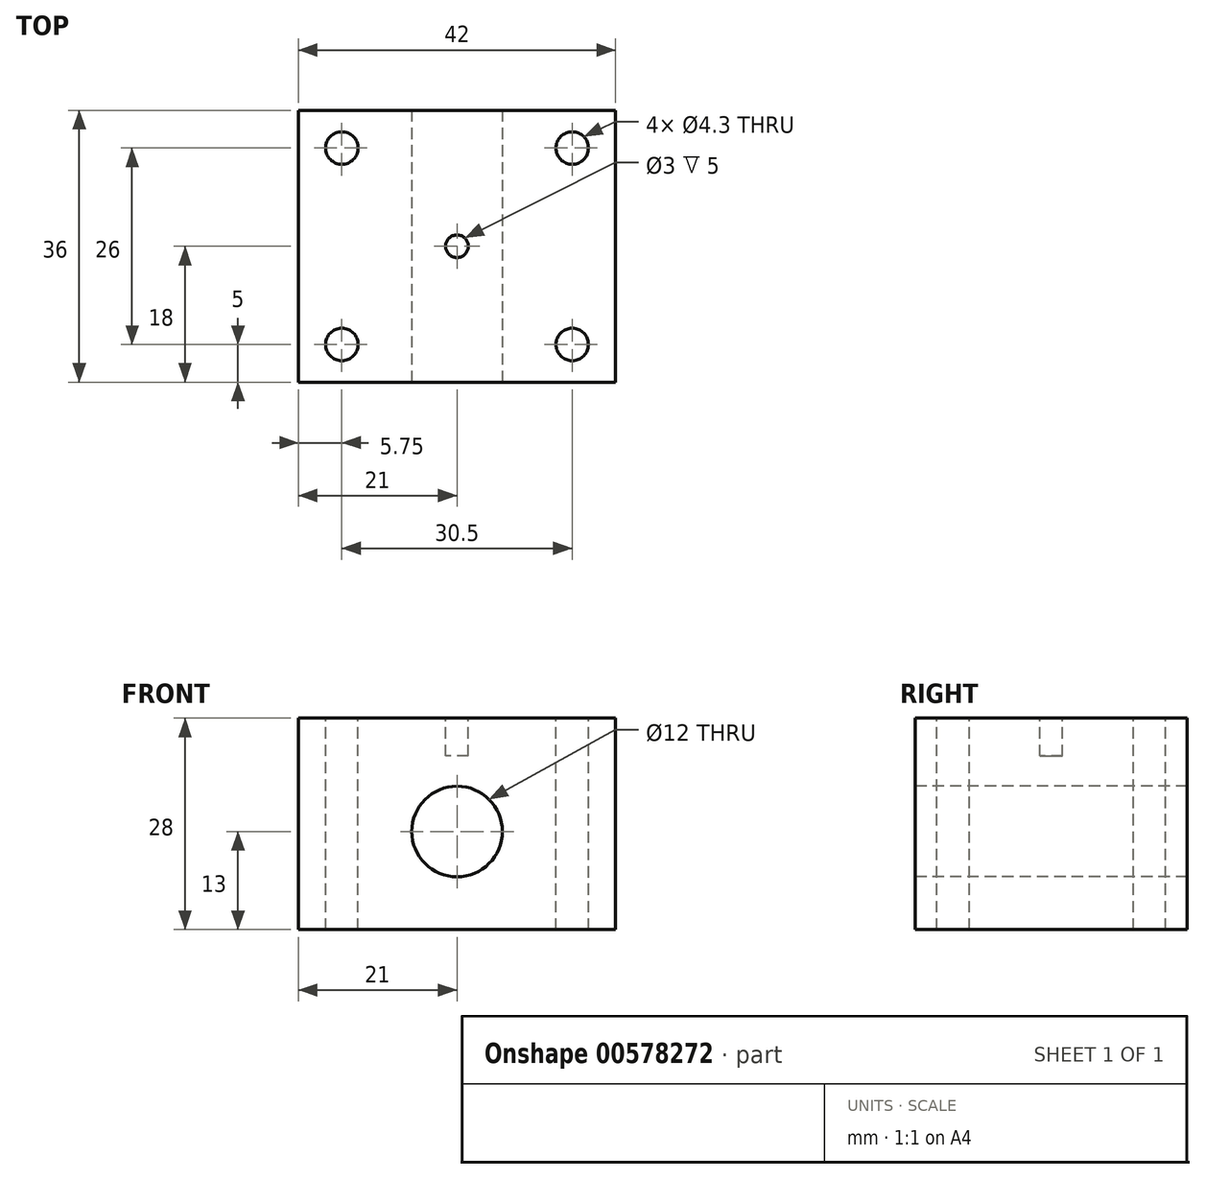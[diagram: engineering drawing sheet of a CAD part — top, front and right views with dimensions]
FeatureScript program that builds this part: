
annotation { "Feature Type Name" : "Feature", "Feature Type Description" : "" }
export const myFeature = defineFeature(function(context is Context, id is Id, definition is map)
    precondition{}
    {
        {
            var Q0;
            Q0=qCreatedBy(makeId("Top.planeOp"),FACE);
            var sketch = newSketch(context, id + "F0", { "sketchPlane" : qUnion([Q0])});
            skLineSegment(sketch, "E0.bottom", {"start": v(-21, 18) * mm, "end": v(21, 18) * mm});
            skLineSegment(sketch, "E0.top", {"start": v(-21, -18) * mm, "end": v(21, -18) * mm});
            skLineSegment(sketch, "E0.left", {"start": v(-21, 18) * mm, "end": v(-21, -18) * mm});
            skLineSegment(sketch, "E0.right", {"start": v(21, 18) * mm, "end": v(21, -18) * mm});
            skPoint(sketch, "E0.middle", {"position": v(0, 0) * mm});
            skCircle(sketch, "E1", {"center": v(-15.25, 13) * mm, "radius": 2.15 * mm});
            skCircle(sketch, "E2.MirrorC", {"center": v(15.25, 13) * mm, "radius": 2.15 * mm});
            skCircle(sketch, "E3.MirrorC", {"center": v(-15.25, -13) * mm, "radius": 2.15 * mm});
            skCircle(sketch, "E4.MirrorC", {"center": v(15.25, -13) * mm, "radius": 2.15 * mm});
            skSolve(sketch);
        }
        {
            var Q0;
            Q0 = qSketchRegion(id + "F0", true);
            extrude(context, id + "F1", {"entities" : qUnion([Q0]), "oppositeDirection" : true, "depth" : 28 * mm, "offsetDistance" : 25 * mm});
        }
        {
            var Q0;
            Q0=makeQuery(id+"F1.opExtrude","SWEPT_FACE",FACE,{"disambiguationData":[OSD([sQuery(id+"F0.wireOp",EDGE,"E0.top")])]});
            var sketch = newSketch(context, id + "F2", { "sketchPlane" : qUnion([Q0])});
            skCircle(sketch, "E5", {"center": v(0, -15) * mm, "radius": 6 * mm});
            skSolve(sketch);
        }
        {
            var Q0;
            Q0 = qSketchRegion(id + "F2", true);
            extrude(context, id + "F3", {"entities" : qUnion([Q0]), "operationType" : NewBodyOperationType.REMOVE, "oppositeDirection" : true, "depth" : 36 * mm, "offsetDistance" : 25 * mm});
        }
        {
            var Q0;
            Q0=makeQuery(id+"F1.opExtrude","CAP_FACE",FACE,{"disambiguationData":[OSD([sQuery(id+"F0.wireOp",EDGE,"E0.bottom"),sQuery(id+"F0.wireOp",EDGE,"E0.top"),sQuery(id+"F0.wireOp",EDGE,"E0.left"),sQuery(id+"F0.wireOp",EDGE,"E0.right"),sQuery(id+"F0.wireOp",EDGE,"E1"),sQuery(id+"F0.wireOp",EDGE,"E2.MirrorC"),sQuery(id+"F0.wireOp",EDGE,"E3.MirrorC"),sQuery(id+"F0.wireOp",EDGE,"E4.MirrorC")])],"isStart":true});
            var sketch = newSketch(context, id + "F4", { "sketchPlane" : qUnion([Q0])});
            skCircle(sketch, "E6", {"center": v(0, 0) * mm, "radius": 1.5 * mm});
            skSolve(sketch);
        }
        {
            var Q0;
            Q0 = qSketchRegion(id + "F4", true);
            extrude(context, id + "F5", {"entities" : qUnion([Q0]), "operationType" : NewBodyOperationType.REMOVE, "oppositeDirection" : true, "depth" : 5 * mm, "offsetDistance" : 25 * mm});
        }
    });
